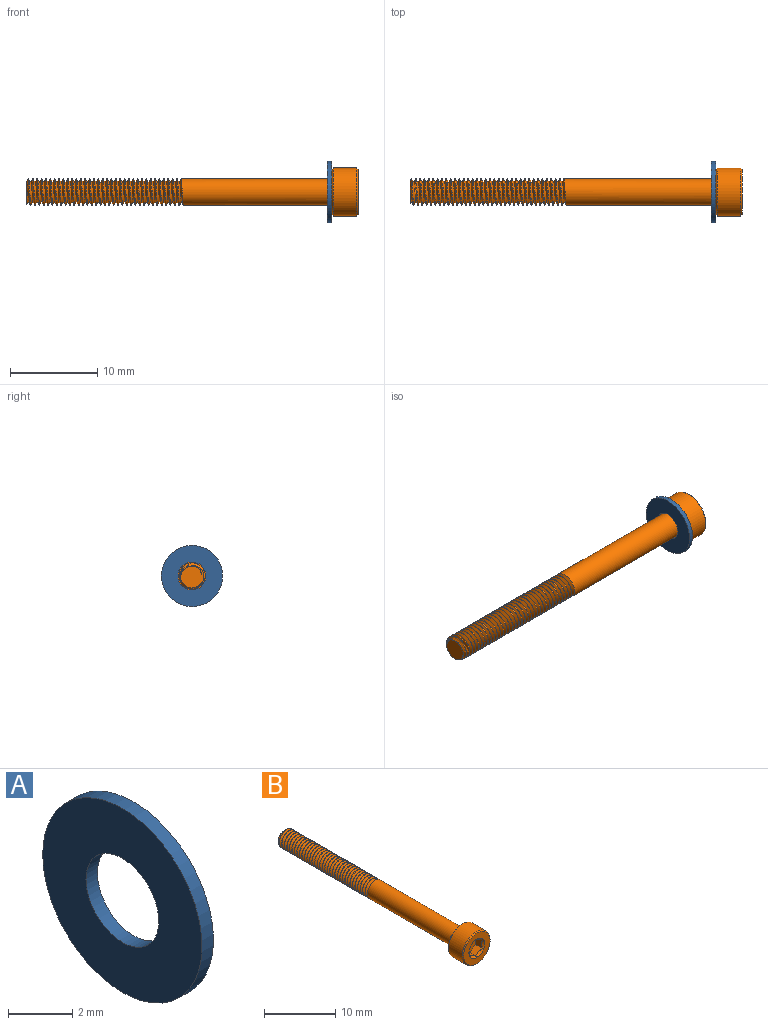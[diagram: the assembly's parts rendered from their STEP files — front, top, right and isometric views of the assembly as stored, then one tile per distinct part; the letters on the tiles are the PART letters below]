
ASSEMBLY  parts=2 mates=1
PART A: 4 faces, bbox 0.5x7x7 mm
  f0: plane 7x7mm, normal (-1,0,0), area 30.4mm2, adj f1,f3
  f1: cylinder r=1.6mm len=3.2mm, axis (1,0,0), area 5mm2, adj f0,f2
  f2: plane 7x7mm, normal (1,0,0), area 30.4mm2, adj f1,f3
  f3: cylinder r=3.5mm len=7mm, axis (1,0,0), area 11mm2, adj f0,f2
PART B: 56 faces, bbox 5.6x38.4x5.6 mm
  f0: cylinder r=1.5mm len=17.63mm, axis (0,1,0), area 162.4mm2, adj f1,f38,f41,f53,f54,f55
  f1: cylinder r=1.5mm len=3mm, axis (0,1,0), area 0.6mm2, adj f0,f2,f54,f55
  f2: cylinder r=1.5mm len=3mm, axis (0,1,0), area 0.6mm2, adj f1,f3,f54,f55
  f3: cylinder r=1.5mm len=3mm, axis (0,1,0), area 0.6mm2, adj f2,f4,f54,f55
  f4: cylinder r=1.5mm len=3mm, axis (0,1,0), area 0.6mm2, adj f3,f5,f54,f55
  f5: cylinder r=1.5mm len=3mm, axis (0,1,0), area 0.6mm2, adj f4,f6,f54,f55
  f6: cylinder r=1.5mm len=3mm, axis (0,1,0), area 0.6mm2, adj f5,f7,f54,f55
  f7: cylinder r=1.5mm len=3mm, axis (0,1,0), area 0.6mm2, adj f6,f8,f54,f55
  f8: cylinder r=1.5mm len=3mm, axis (0,1,0), area 0.6mm2, adj f7,f9,f54,f55
  f9: cylinder r=1.5mm len=3mm, axis (0,1,0), area 0.6mm2, adj f8,f10,f54,f55
  f10: cylinder r=1.5mm len=3mm, axis (0,1,0), area 0.6mm2, adj f9,f11,f54,f55
  f11: cylinder r=1.5mm len=3mm, axis (0,1,0), area 0.6mm2, adj f10,f12,f54,f55
  f12: cylinder r=1.5mm len=3mm, axis (0,1,0), area 0.6mm2, adj f11,f13,f54,f55
  f13: cylinder r=1.5mm len=3mm, axis (0,1,0), area 0.6mm2, adj f12,f14,f54,f55
  f14: cylinder r=1.5mm len=3mm, axis (0,1,0), area 0.6mm2, adj f13,f15,f54,f55
  f15: cylinder r=1.5mm len=3mm, axis (0,1,0), area 0.6mm2, adj f14,f16,f54,f55
  f16: cylinder r=1.5mm len=3mm, axis (0,1,0), area 0.6mm2, adj f15,f17,f54,f55
  f17: cylinder r=1.5mm len=3mm, axis (0,1,0), area 0.6mm2, adj f16,f18,f54,f55
  f18: cylinder r=1.5mm len=3mm, axis (0,1,0), area 0.6mm2, adj f17,f19,f54,f55
  f19: cylinder r=1.5mm len=3mm, axis (0,1,0), area 0.6mm2, adj f18,f20,f54,f55
  f20: cylinder r=1.5mm len=3mm, axis (0,1,0), area 0.6mm2, adj f19,f21,f54,f55
  f21: cylinder r=1.5mm len=3mm, axis (0,1,0), area 0.6mm2, adj f20,f22,f54,f55
  f22: cylinder r=1.5mm len=3mm, axis (0,1,0), area 0.6mm2, adj f21,f23,f54,f55
  f23: cylinder r=1.5mm len=3mm, axis (0,1,0), area 0.6mm2, adj f22,f24,f54,f55
  f24: cylinder r=1.5mm len=3mm, axis (0,1,0), area 0.6mm2, adj f23,f25,f54,f55
  f25: cylinder r=1.5mm len=3mm, axis (0,1,0), area 0.6mm2, adj f24,f26,f54,f55
  f26: cylinder r=1.5mm len=3mm, axis (0,1,0), area 0.6mm2, adj f25,f27,f54,f55
  f27: cylinder r=1.5mm len=3mm, axis (0,1,0), area 0.6mm2, adj f26,f28,f54,f55
  f28: cylinder r=1.5mm len=3mm, axis (0,1,0), area 0.6mm2, adj f27,f29,f54,f55
  f29: cylinder r=1.5mm len=3mm, axis (0,1,0), area 0.6mm2, adj f28,f30,f54,f55
  f30: cylinder r=1.5mm len=3mm, axis (0,1,0), area 0.6mm2, adj f29,f31,f54,f55
  f31: cylinder r=1.5mm len=3mm, axis (0,1,0), area 0.6mm2, adj f30,f32,f54,f55
  f32: cylinder r=1.5mm len=3mm, axis (0,1,0), area 0.6mm2, adj f31,f33,f54,f55
  f33: cylinder r=1.5mm len=3mm, axis (0,1,0), area 0.6mm2, adj f32,f34,f54,f55
  f34: cylinder r=1.5mm len=3mm, axis (0,1,0), area 0.6mm2, adj f33,f35,f54,f55
  f35: cylinder r=1.5mm len=3mm, axis (0,1,0), area 0.3mm2, adj f34,f37,f54,f55
  f36: plane 2.75x2.64mm, normal (0,1,0), area 5.2mm2, adj f37,f54,f55
  f37: cone r=1.35mm half-angle=45deg, axis (0,-1,0), area 0.5mm2, adj f35,f36,f54,f55
  f38: plane 1x0.38mm, normal (0,-0.87,-0.5), area 0.3mm2, adj f0,f53,f54
  f39: cylinder r=2.75mm len=5.5mm, axis (0,1,0), area 46.7mm2, adj f51,f52
  f40: plane 5.2x5.2mm, normal (0,-1,0), area 13.5mm2, adj f42,f52
  f41: plane 5.2x5.2mm, normal (0,1,0), area 14.2mm2, adj f0,f51
  f42: cone r=1.57mm half-angle=45deg, axis (0,-1,0), area 3.2mm2, adj f40,f44,f45,f46,f47,f48,f49
  f43: plane 2.89x2.5mm, normal (0,-1,0), area 5.4mm2, adj f44,f45,f46,f47,f48,f49,f50
  f44: plane 1.59x1.52mm, normal (-1,0,0), area 1.8mm2, adj f42,f43,f45,f49
  f45: plane 1.38x1.25mm, normal (-0.5,0,0.87), area 1.8mm2, adj f42,f43,f44,f46
  f46: plane 1.38x1.25mm, normal (0.5,0,0.87), area 1.8mm2, adj f42,f43,f45,f47
  f47: plane 1.45x1.38mm, normal (1,0,0), area 1.8mm2, adj f42,f43,f46,f48
  f48: plane 1.38x1.25mm, normal (0.5,0,-0.87), area 1.8mm2, adj f42,f43,f47,f49
  f49: plane 1.38x1.25mm, normal (-0.5,0,-0.87), area 1.8mm2, adj f42,f43,f44,f48
  f50: cone r=1.57mm half-angle=45deg, axis (0,-1,0), area 0mm2, adj f43
  f51: cone r=2.6mm half-angle=45deg, axis (0,-1,0), area 3.6mm2, adj f39,f41
  f52: cone r=2.75mm half-angle=45deg, axis (0,1,0), area 3.6mm2, adj f39,f40
  f53: plane 1.28x0.4mm, normal (0,0.87,-0.5), area 0.4mm2, adj f0,f38,f55
  f54: bspline ~18.05x3.46mm, area 127.9mm2, adj f0,f1,f2,f3,f4,f5,f6,f7
  f55: bspline ~18.14x3.46mm, area 129.4mm2, adj f0,f1,f2,f3,f4,f5,f6,f7
PLACE A at identity fixed
PLACE B rot(axis=(0,0,1),90deg) t=(-34.5,0,0)mm
MATE fastened B.f0 <-> A.f1  axis (-1,0,0) through (0.5,0,0)mm
